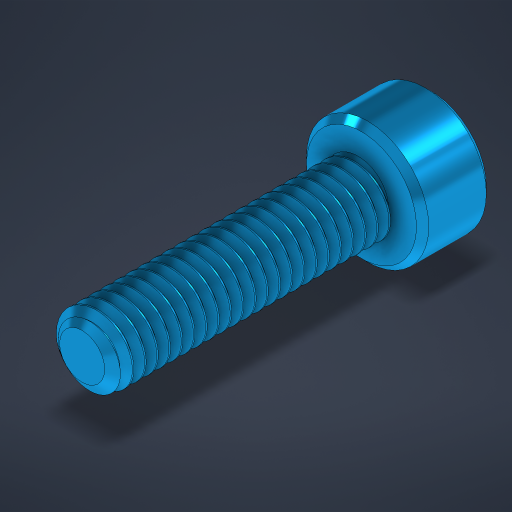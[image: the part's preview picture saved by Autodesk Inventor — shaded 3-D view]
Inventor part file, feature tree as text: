
AUTODESK INVENTOR PART (.ipt)
format: ipt  version: 2024 (Build 280153000, 153)  size: 920,064 bytes
history: native  units: in
note: dims shown in document units (in); Inventor stores cm internally (conversion verified against a paired STEP export)
features: chamfer x1
ambient origin geometry x8: Origin, YZ Plane, XZ Plane, XY Plane, X Axis, Y Axis, Z Axis, Center Point
bodies: Solid1 (feature_tree)
feature tree (1):
  chamfer  "Chamfer1"  [1 undecoded]
note: 1 required parameter value undecoded (feature->parameter linkage not recoverable at this tier; creation-order binding heuristic only, values carry confidence <= 0.55)
